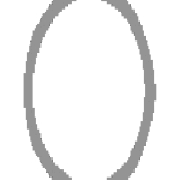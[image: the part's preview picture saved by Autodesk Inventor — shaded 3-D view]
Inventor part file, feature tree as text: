
AUTODESK INVENTOR PART (.ipt)
format: ipt  version: 2021 (Build 250183000, 183)  size: 109,056 bytes
history: native  units: in
note: dims shown in document units (in); Inventor stores cm internally (conversion verified against a paired STEP export)
features: other x4, sketch x3, plane x1
ambient origin geometry x8: Origin, YZ Plane, XZ Plane, XY Plane, X Axis, Y Axis, Z Axis, Center Point
bodies: Solid1 (feature_tree), Body (feature_tree)
feature tree (8):
  other  "Driven Length"
  other  "Frame Generator"
  other  "Start Plane"
  other  "End Plane"
  sketch  "Sketch"  dims[d2=40.658in d4=-0.0in d5=40.658in d6=0.12in d7=0.0in d8=90.0deg d9=40.658in]
  sketch  "Sketch2"  dims[d0=1.0in]
  plane  "Work Plane3"
  sketch  "Sketch3"  dims[d1=0.065in]
